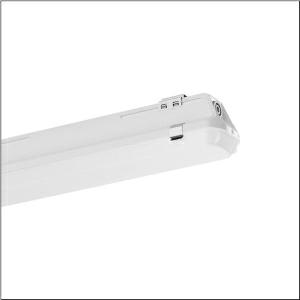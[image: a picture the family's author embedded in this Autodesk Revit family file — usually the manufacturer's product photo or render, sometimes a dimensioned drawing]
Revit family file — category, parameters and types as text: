
# Revit family: monsun_r__11_51fp109p460h_b614
name_source: partatom
category: Lighting Fixtures
units: mm (PartAtom-declared; Revit-internal decimal feet)

## family parameters
Cut with Voids When Loaded = No
Host = Face
Light Source = No
Part Type = Normal
Room Calculation Point = No
Round Connector Dimension = Use Diameter
Shared = No

## types (1)
- Monsun® 11 (1 x LED, 6100 lm, 34 W, 4000K)
    Apparent Load = 34 VA
    CIE Flux Codes = 47 77 93 94 100
    Color Rendering = 80
    Color Temperature = 4000K
    Default Elevation = 1800 mm
    Description = Monsun® 11, damp-proof luminaire, chain hanger, primary optical cover: enclosure, of PMMA, light emission: direct distribution, primary light characteristic: symmetric, installation type: suspended mounting, surface-mounted, horizontal mounting, vertical mounting, LED, rated luminous flux: 6.100lm, luminous efficacy: 179lm/W, light colour: 840, colour temperature: 4000K, control gear: ECG, with terminal, 3-pole, max. 2.5mm², mains connection: 220..240V, AC, 50/60Hz, start of lifetime: 34W, end of service life: 38W, luminaire housing, of glass-fibre reinforced polyester, uncoated, bright grey, incl. chain hanger, length: 1.590mm, width: 90mm, height: 88mm, clip for enclosure, of stainless steel (V2A), ceiling mounting element, of stainless steel (V2A), chain hanger, of stainless steel (V2A), protection rating (complete): IP66, insulation class (complete): insulation class I (protective earthing), certification: CE, ENEC, VDE, UKCA, protection symbol: D, impact resistance: IK04, permissible operating ambient temperature: -35..+40°C, standard: EN 50419, EN 60598-2-1, no direct snow, no direct sun, no direct rain, for indoor or canopied outdoor use, corresponds to IFS (International Featured Standards) requirements for safety and quality in the food industry, contact your sales advisor before using the luminaires in applications with unclear chemical exposure, large temperature fluctuations or condensation-forming humidity, LABS conformity tested according to VDMA 24364:2018-05, packaging unit: 1 piece
    Height = 89 mm
    Lamp = 1 x LED
    Lamp Light Flux = 6100 lm
    Lamp Power = 34 W
    Lamp count = 1
    Length = 1590 mm
    Luminous efficacy = 179 lm/W
    Manufacturer = Siteco
    ModVariant = No
    Model = 51FP109P460H
    Mounting Place = Ceiling
    Mounting Type = Surface mounted
    Number of Poles = 1
    OnlyDefault = Yes
    Power Factor = 1
    Product Name = Monsun® 11
    Product group = damp-proof luminaire
    ProductGroupID = 301
    Protection Class = Protection class I
    Protection Degree = IP 66
    RLX_Detail_Level = 1
    RLX_Emergency_Light_Flux = 0 lm
    RLX_Emergency_Type = 0
    RLX_Emergency_Type_DB = No
    RlxData = <blob elided: 88749 chars, md5=fd76fb50>
    Socket = socket
    Standby Power = 0 W
    System Light Flux = 6100 lm
    System Power = 34 W
    Type Comments = Product without accessories
    Type Image = l_1004748.jpg
    URL = http://relux.com
    VarID = ---
    Voltage = 0 V
    Weight = 0.00 kg
    Width = 90 mm

## geometry (parser evidence)
native form markers: Blend x4, Sweep x13
no freeform markers — native parametric forms only
